# Revit family: Faucet-Lavatory-Delta-Trinsic-Wide_Wall
name_source: partatom
category: Plumbing Fixtures
revit_build: Autodesk Revit MEP 2012 (Build: 20110916_2132(x64)
units: mm (PartAtom-declared; Revit-internal decimal feet)

## types (2) — shared parameters
Date Modified = July 17, 2015
Default Elevation = 48 "
Depth = 2 "
Equipment Abbreviation = KF
Family Version = 1.0
Height = 7 "
Manufacturer = Delta Faucet Company
Model Disclaimer = Contact Delta Faucet Company for More Information
Product Documentation Link = http://www.deltafaucet.com
Product Page URL = http://www.deltafaucet.com
URL = http://www.deltafaucet.com
z Depth = 7 "
z Width = 11.64 "

## per-type parameters (varying)
| type | Description | Model | Product Material | z Type |
| Chrome | Compel Two Handle Wall Mount Lavatory, Chrome | T3561LF-WL | Chrome - Delta - Polished | 1 |
| Stainless | Compel Two Handle Wall Mount Lavatory, Stainless | T3561LF-SSWL | Stainless Steel - Delta - Polished | 4 |

## geometry (parser evidence)
native form markers: Blend x4, Sweep x2
no freeform markers — native parametric forms only
